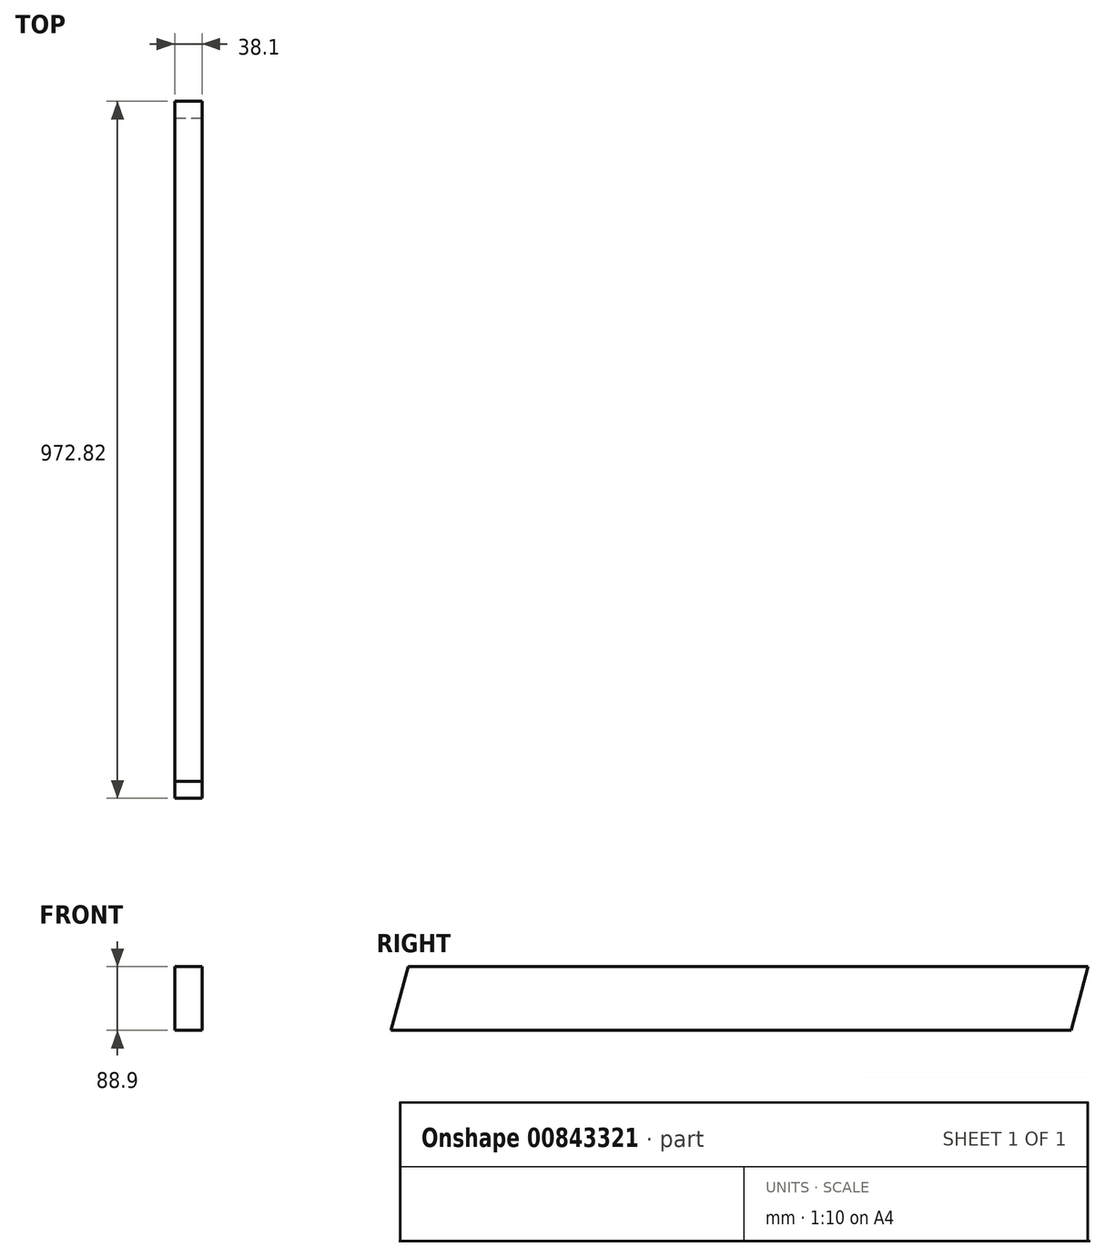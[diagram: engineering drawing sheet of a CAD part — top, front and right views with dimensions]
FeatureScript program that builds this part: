
annotation { "Feature Type Name" : "Feature", "Feature Type Description" : "" }
export const myFeature = defineFeature(function(context is Context, id is Id, definition is map)
    precondition{}
    {
        {
            var Q0;
            Q0=qCreatedBy(makeId("Front.planeOp"),FACE);
            var sketch = newSketch(context, id + "F0", { "sketchPlane" : qUnion([Q0])});
            skLineSegment(sketch, "E0.bottom", {"start": v(19.05, -44.45) * mm, "end": v(-19.05, -44.45) * mm});
            skLineSegment(sketch, "E0.top", {"start": v(19.05, 44.45) * mm, "end": v(-19.05, 44.45) * mm});
            skLineSegment(sketch, "E0.left", {"start": v(19.05, -44.45) * mm, "end": v(19.05, 44.45) * mm});
            skLineSegment(sketch, "E0.right", {"start": v(-19.05, -44.45) * mm, "end": v(-19.05, 44.45) * mm});
            skPoint(sketch, "E0.middle", {"position": v(0, 0) * mm});
            skSolve(sketch);
        }
        {
            var Q0;
            Q0=makeQuery(id+"F0.imprint","IMPRINT",FACE,{"disambiguationData":[TD([[makeQuery(id+"F0.imprint","IMPRINT",EDGE,{"derivedFrom":sQuery(id+"F0.wireOp",EDGE,"E0.bottom")}),-1.0]])]});
            extrude(context, id + "F1", {"entities" : qUnion([Q0]), "depth" : 972.82 * mm, "offsetDistance" : 25.4 * mm});
        }
        {
            var Q0;
            Q0=qCreatedBy(makeId("Right.planeOp"),FACE);
            var sketch = newSketch(context, id + "F2", { "sketchPlane" : qUnion([Q0])});
            skLineSegment(sketch, "E1", {"start": v(-948.94, 44.45) * mm, "end": v(-972.82, 44.45) * mm});
            skLineSegment(sketch, "E2", {"start": v(-972.82, 44.45) * mm, "end": v(-972.82, -44.45) * mm});
            skLineSegment(sketch, "E3", {"start": v(-972.82, -44.45) * mm, "end": v(-948.94, 44.45) * mm});
            skSolve(sketch);
        }
        {
            var Q0;
            Q0 = qSketchRegion(id + "F2", true);
            extrude(context, id + "F3", {"entities" : qUnion([Q0]), "operationType" : NewBodyOperationType.REMOVE, "oppositeDirection" : true, "depth" : 50.8 * mm, "offsetDistance" : 25.4 * mm, "symmetric" : true});
        }
        {
            var Q0;
            Q0=qCreatedBy(makeId("Right.planeOp"),FACE);
            var sketch = newSketch(context, id + "F4", { "sketchPlane" : qUnion([Q0])});
            skLineSegment(sketch, "E4", {"start": v(0, 44.45) * mm, "end": v(-23.88, -44.45) * mm});
            skLineSegment(sketch, "E5", {"start": v(-23.88, -44.45) * mm, "end": v(0, -44.45) * mm});
            skLineSegment(sketch, "E6", {"start": v(0, -44.45) * mm, "end": v(0, 44.45) * mm});
            skSolve(sketch);
        }
        {
            var Q0;
            Q0 = qSketchRegion(id + "F4", true);
            extrude(context, id + "F5", {"entities" : qUnion([Q0]), "operationType" : NewBodyOperationType.REMOVE, "depth" : 50.8 * mm, "offsetDistance" : 25.4 * mm, "symmetric" : true});
        }
    });
